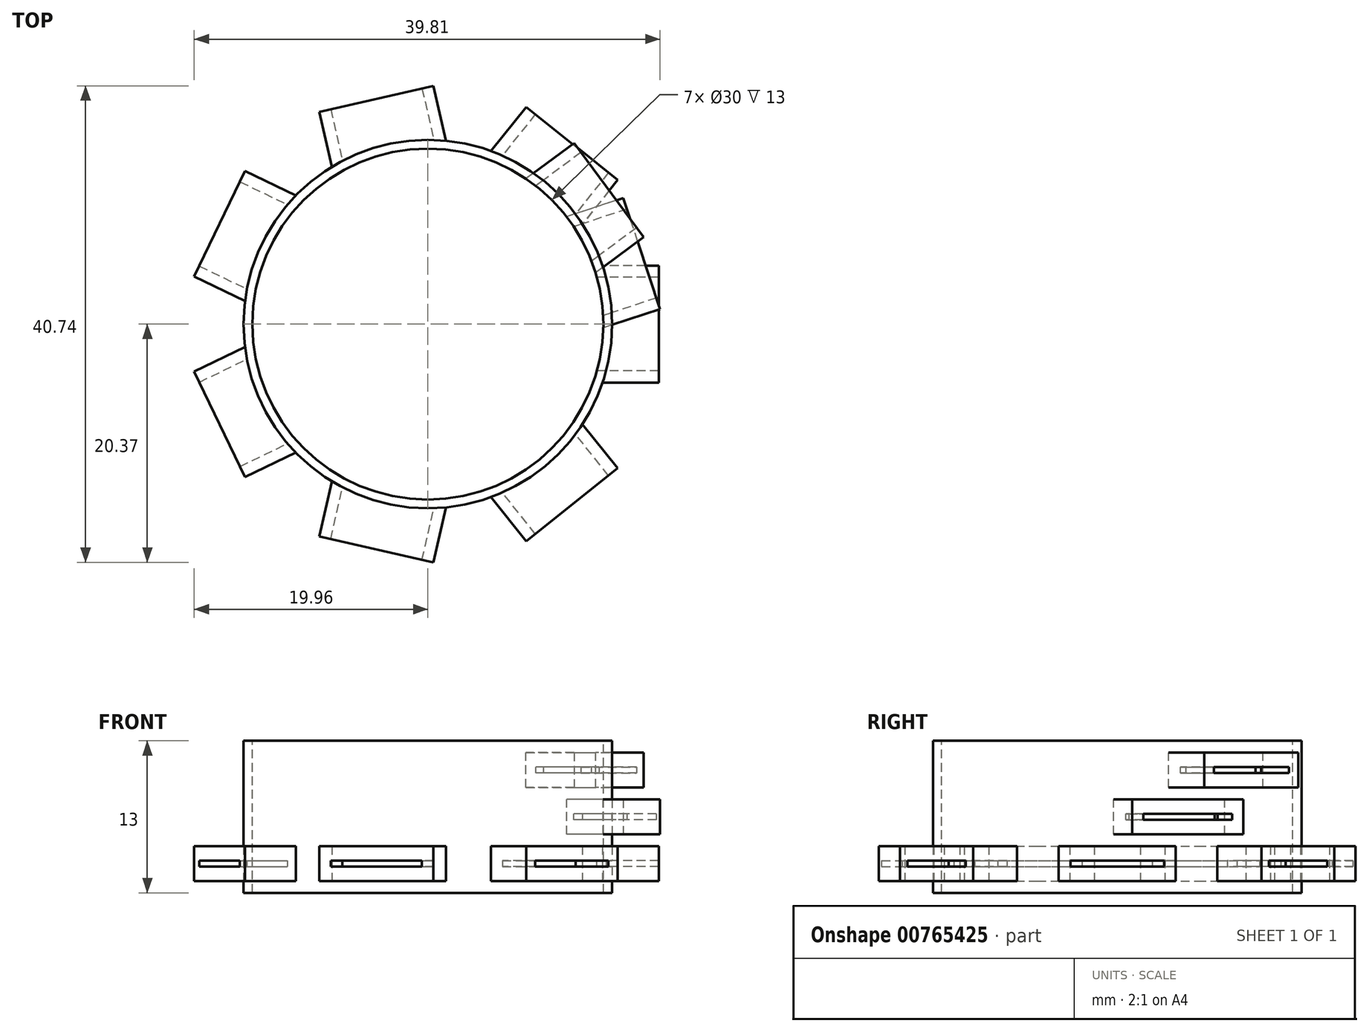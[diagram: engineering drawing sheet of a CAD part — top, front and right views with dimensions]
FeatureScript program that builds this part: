
annotation { "Feature Type Name" : "Feature", "Feature Type Description" : "" }
export const myFeature = defineFeature(function(context is Context, id is Id, definition is map)
    precondition{}
    {
        {
            var Q0;
            Q0=qCreatedBy(makeId("Top.planeOp"),FACE);
            var sketch = newSketch(context, id + "F0", { "sketchPlane" : qUnion([Q0])});
            skCircle(sketch, "E0", {"center": v(0, 0) * mm, "radius": 15.75 * mm});
            skSolve(sketch);
        }
        {
            var Q0;
            Q0 = qSketchRegion(id + "F0", true);
            extrude(context, id + "F1", {"entities" : qUnion([Q0]), "depth" : 13 * mm, "offsetDistance" : 25 * mm});
        }
        {
            var Q0;
            Q0=qCreatedBy(makeId("Right.planeOp"),FACE);
            var sketch = newSketch(context, id + "F2", { "sketchPlane" : qUnion([Q0])});
            skLineSegment(sketch, "E1.bottom", {"start": v(5, 4) * mm, "end": v(-5, 4) * mm});
            skLineSegment(sketch, "E1.top", {"start": v(5, 1) * mm, "end": v(-5, 1) * mm});
            skLineSegment(sketch, "E1.left", {"start": v(5, 4) * mm, "end": v(5, 1) * mm});
            skLineSegment(sketch, "E1.right", {"start": v(-5, 4) * mm, "end": v(-5, 1) * mm});
            skLineSegment(sketch, "E2", {"start": v(0, 0) * mm, "end": v(0, 1) * mm, "construction": true});
            skLineSegment(sketch, "E3.bottom", {"start": v(4, 2.75) * mm, "end": v(-4, 2.75) * mm});
            skLineSegment(sketch, "E3.top", {"start": v(4, 2.25) * mm, "end": v(-4, 2.25) * mm});
            skLineSegment(sketch, "E3.left", {"start": v(4, 2.75) * mm, "end": v(4, 2.25) * mm});
            skLineSegment(sketch, "E3.right", {"start": v(-4, 2.75) * mm, "end": v(-4, 2.25) * mm});
            skLineSegment(sketch, "E4", {"start": v(-5, 2.5) * mm, "end": v(5, 2.5) * mm, "construction": true});
            skLineSegment(sketch, "E5", {"start": v(-4, 2.5) * mm, "end": v(4, 2.5) * mm, "construction": true});
            skLineSegment(sketch, "E6", {"start": v(-4, 2.75) * mm, "end": v(-5, 2.75) * mm, "construction": true});
            skLineSegment(sketch, "E7", {"start": v(4, 2.75) * mm, "end": v(5, 2.75) * mm, "construction": true});
            skSolve(sketch);
        }
        {
            var Q0;
            Q0 = qSketchRegion(id + "F2", true);
            extrude(context, id + "F3", {"entities" : qUnion([Q0]), "operationType" : NewBodyOperationType.ADD, "depth" : 19.75 * mm, "offsetDistance" : 25 * mm});
        }
        {
            var Q0;
            Q0=qCreatedBy(makeId("Front.planeOp"),FACE);
            var sketch = newSketch(context, id + "F4", { "sketchPlane" : qUnion([Q0])});
            skLineSegment(sketch, "E8", {"start": v(0, 0) * mm, "end": v(0, 43.97) * mm, "construction": true});
            skSolve(sketch);
        }
        {
            var Q0;
            Q0=makeQuery(id+"F1.opExtrude","SWEPT_BODY",BODY,{"disambiguationData":[OSD([sQuery(id+"F0.wireOp",EDGE,"E0")])]});
            var Q1;
            Q1=sQuery(id+"F4.wireOp",EDGE,"E8");
            circularPattern(context, id + "F5", {"entities" : qUnion([Q0]), "axis" : qUnion([Q1]), "angle" : 360 * degree, "instanceCount" : 7, "equalSpace" : true});
        }
        {
            var Q0;
            Q0=qCreatedBy(makeId("Top.planeOp"),FACE);
            var sketch = newSketch(context, id + "F6", { "sketchPlane" : qUnion([Q0])});
            skLineSegment(sketch, "E9", {"start": v(0, 0) * mm, "end": v(32.43, 0) * mm, "construction": true});
            skLineSegment(sketch, "E10", {"start": v(0, 0) * mm, "end": v(32.64, 10.77) * mm, "construction": true});
            skLineSegment(sketch, "E11", {"start": v(0, 0) * mm, "end": v(-3.5, 10.6) * mm, "construction": true});
            skLineSegment(sketch, "E12", {"start": v(0, 0) * mm, "end": v(19.96, 14.8) * mm, "construction": true});
            skLineSegment(sketch, "E13", {"start": v(0, 0) * mm, "end": v(-17.15, 23.15) * mm, "construction": true});
            skSolve(sketch);
        }
        {
            var Q0;
            Q0=sQuery(id+"F6.wireOp",EDGE,"E11");
            cPlane(context, id + "F7", {"entities" : qUnion([Q0]), "cplaneType" : CPlaneType.LINE_ANGLE, "offset" : 25 * mm, "angle" : 90 * degree, "oppositeDirection" : true, "width" : 150 * mm, "height" : 150 * mm});
        }
        {
            var Q0;
            Q0=qCreatedBy(id+"F7.planeOp",FACE);
            var sketch = newSketch(context, id + "F8", { "sketchPlane" : qUnion([Q0])});
            skLineSegment(sketch, "E14.bottom", {"start": v(5, 8) * mm, "end": v(-5, 8) * mm});
            skLineSegment(sketch, "E14.top", {"start": v(5, 5) * mm, "end": v(-5, 5) * mm});
            skLineSegment(sketch, "E14.left", {"start": v(5, 8) * mm, "end": v(5, 5) * mm});
            skLineSegment(sketch, "E14.right", {"start": v(-5, 8) * mm, "end": v(-5, 5) * mm});
            skLineSegment(sketch, "E15", {"start": v(0, 0) * mm, "end": v(0, 5) * mm, "construction": true});
            skLineSegment(sketch, "E16.bottom", {"start": v(4, 6.75) * mm, "end": v(-4, 6.75) * mm});
            skLineSegment(sketch, "E16.top", {"start": v(4, 6.25) * mm, "end": v(-4, 6.25) * mm});
            skLineSegment(sketch, "E16.left", {"start": v(4, 6.75) * mm, "end": v(4, 6.25) * mm});
            skLineSegment(sketch, "E16.right", {"start": v(-4, 6.75) * mm, "end": v(-4, 6.25) * mm});
            skLineSegment(sketch, "E17", {"start": v(4, 6.5) * mm, "end": v(-4, 6.5) * mm, "construction": true});
            skLineSegment(sketch, "E18", {"start": v(5, 6.5) * mm, "end": v(-5, 6.5) * mm, "construction": true});
            skLineSegment(sketch, "E19", {"start": v(-4, 6.75) * mm, "end": v(-5, 6.75) * mm, "construction": true});
            skLineSegment(sketch, "E20", {"start": v(4, 6.75) * mm, "end": v(5, 6.75) * mm, "construction": true});
            skSolve(sketch);
        }
        {
            var Q0;
            Q0 = qSketchRegion(id + "F8", true);
            extrude(context, id + "F9", {"entities" : qUnion([Q0]), "oppositeDirection" : true, "depth" : 19.25 * mm, "offsetDistance" : 25 * mm});
        }
        {
            var Q0;
            Q0=sQuery(id+"F6.wireOp",EDGE,"E13");
            cPlane(context, id + "F10", {"entities" : qUnion([Q0]), "cplaneType" : CPlaneType.LINE_ANGLE, "offset" : 25 * mm, "angle" : 90 * degree, "oppositeDirection" : true, "width" : 150 * mm, "height" : 150 * mm});
        }
        {
            var Q0;
            Q0=qCreatedBy(id+"F10.planeOp",FACE);
            var sketch = newSketch(context, id + "F11", { "sketchPlane" : qUnion([Q0])});
            skLineSegment(sketch, "E21", {"start": v(0, 0) * mm, "end": v(0, 9) * mm, "construction": true});
            skLineSegment(sketch, "E22.bottom", {"start": v(-5, 12) * mm, "end": v(5, 12) * mm});
            skLineSegment(sketch, "E22.top", {"start": v(-5, 9) * mm, "end": v(5, 9) * mm});
            skLineSegment(sketch, "E22.left", {"start": v(-5, 12) * mm, "end": v(-5, 9) * mm});
            skLineSegment(sketch, "E22.right", {"start": v(5, 12) * mm, "end": v(5, 9) * mm});
            skLineSegment(sketch, "E23", {"start": v(-5, 10.5) * mm, "end": v(5, 10.5) * mm, "construction": true});
            skLineSegment(sketch, "E24.bottom", {"start": v(-4, 10.75) * mm, "end": v(4, 10.75) * mm});
            skLineSegment(sketch, "E24.top", {"start": v(-4, 10.25) * mm, "end": v(4, 10.25) * mm});
            skLineSegment(sketch, "E24.left", {"start": v(-4, 10.75) * mm, "end": v(-4, 10.25) * mm});
            skLineSegment(sketch, "E24.right", {"start": v(4, 10.75) * mm, "end": v(4, 10.25) * mm});
            skLineSegment(sketch, "E25", {"start": v(-4, 10.5) * mm, "end": v(4, 10.5) * mm, "construction": true});
            skLineSegment(sketch, "E26", {"start": v(-4, 10.75) * mm, "end": v(-5, 10.75) * mm, "construction": true});
            skLineSegment(sketch, "E27", {"start": v(4, 10.75) * mm, "end": v(5, 10.75) * mm, "construction": true});
            skSolve(sketch);
        }
        {
            var Q0;
            Q0 = qSketchRegion(id + "F11", true);
            extrude(context, id + "F12", {"entities" : qUnion([Q0]), "oppositeDirection" : true, "depth" : 19.25 * mm, "offsetDistance" : 25 * mm});
        }
        {
            var Q0;
            Q0=makeQuery(id+"F5.opPattern","COPY",FACE,{"derivedFrom":makeQuery(id+"F1.opExtrude","CAP_FACE",FACE,{"disambiguationData":[OSD([sQuery(id+"F0.wireOp",EDGE,"E0")])],"isStart":false}),"instanceName":"3"});
            var sketch = newSketch(context, id + "F13", { "sketchPlane" : qUnion([Q0])});
            skCircle(sketch, "E28", {"center": v(0, 0) * mm, "radius": 15 * mm});
            skSolve(sketch);
        }
        {
            var Q0;
            Q0 = qSketchRegion(id + "F13", true);
            extrude(context, id + "F14", {"entities" : qUnion([Q0]), "operationType" : NewBodyOperationType.REMOVE, "oppositeDirection" : true, "depth" : 30 * mm, "offsetDistance" : 25 * mm});
        }
        {
            var Q0;
            Q0=qCreatedBy(makeId("Right.planeOp"),FACE);
            var sketch = newSketch(context, id + "F15", { "sketchPlane" : qUnion([Q0])});
            skLineSegment(sketch, "E29.bottom", {"start": v(-4, 2.75) * mm, "end": v(4, 2.75) * mm});
            skLineSegment(sketch, "E29.top", {"start": v(-4, 2.25) * mm, "end": v(4, 2.25) * mm});
            skLineSegment(sketch, "E29.left", {"start": v(-4, 2.75) * mm, "end": v(-4, 2.25) * mm});
            skLineSegment(sketch, "E29.right", {"start": v(4, 2.75) * mm, "end": v(4, 2.25) * mm});
            skSolve(sketch);
        }
        {
            var Q0;
            Q0 = qSketchRegion(id + "F15", true);
            extrude(context, id + "F16", {"entities" : qUnion([Q0]), "operationType" : NewBodyOperationType.REMOVE, "depth" : 25 * mm, "offsetDistance" : 25 * mm});
        }
        {
            var Q0;
            Q0=qCreatedBy(id+"F7.planeOp",FACE);
            var sketch = newSketch(context, id + "F17", { "sketchPlane" : qUnion([Q0])});
            skLineSegment(sketch, "E30.bottom", {"start": v(4, 6.75) * mm, "end": v(-4, 6.75) * mm});
            skLineSegment(sketch, "E30.top", {"start": v(4, 6.25) * mm, "end": v(-4, 6.25) * mm});
            skLineSegment(sketch, "E30.left", {"start": v(4, 6.75) * mm, "end": v(4, 6.25) * mm});
            skLineSegment(sketch, "E30.right", {"start": v(-4, 6.75) * mm, "end": v(-4, 6.25) * mm});
            skSolve(sketch);
        }
        {
            var Q0;
            Q0 = qSketchRegion(id + "F17", true);
            extrude(context, id + "F18", {"entities" : qUnion([Q0]), "operationType" : NewBodyOperationType.REMOVE, "oppositeDirection" : true, "depth" : 25 * mm, "offsetDistance" : 25 * mm});
        }
        {
            var Q0;
            Q0=qCreatedBy(id+"F10.planeOp",FACE);
            var sketch = newSketch(context, id + "F19", { "sketchPlane" : qUnion([Q0])});
            skLineSegment(sketch, "E31.bottom", {"start": v(4, 10.75) * mm, "end": v(-4, 10.75) * mm});
            skLineSegment(sketch, "E31.top", {"start": v(4, 10.25) * mm, "end": v(-4, 10.25) * mm});
            skLineSegment(sketch, "E31.left", {"start": v(4, 10.75) * mm, "end": v(4, 10.25) * mm});
            skLineSegment(sketch, "E31.right", {"start": v(-4, 10.75) * mm, "end": v(-4, 10.25) * mm});
            skSolve(sketch);
        }
        {
            var Q0;
            Q0 = qSketchRegion(id + "F19", true);
            extrude(context, id + "F20", {"entities" : qUnion([Q0]), "operationType" : NewBodyOperationType.REMOVE, "oppositeDirection" : true, "depth" : 25 * mm, "offsetDistance" : 25 * mm});
        }
    });
